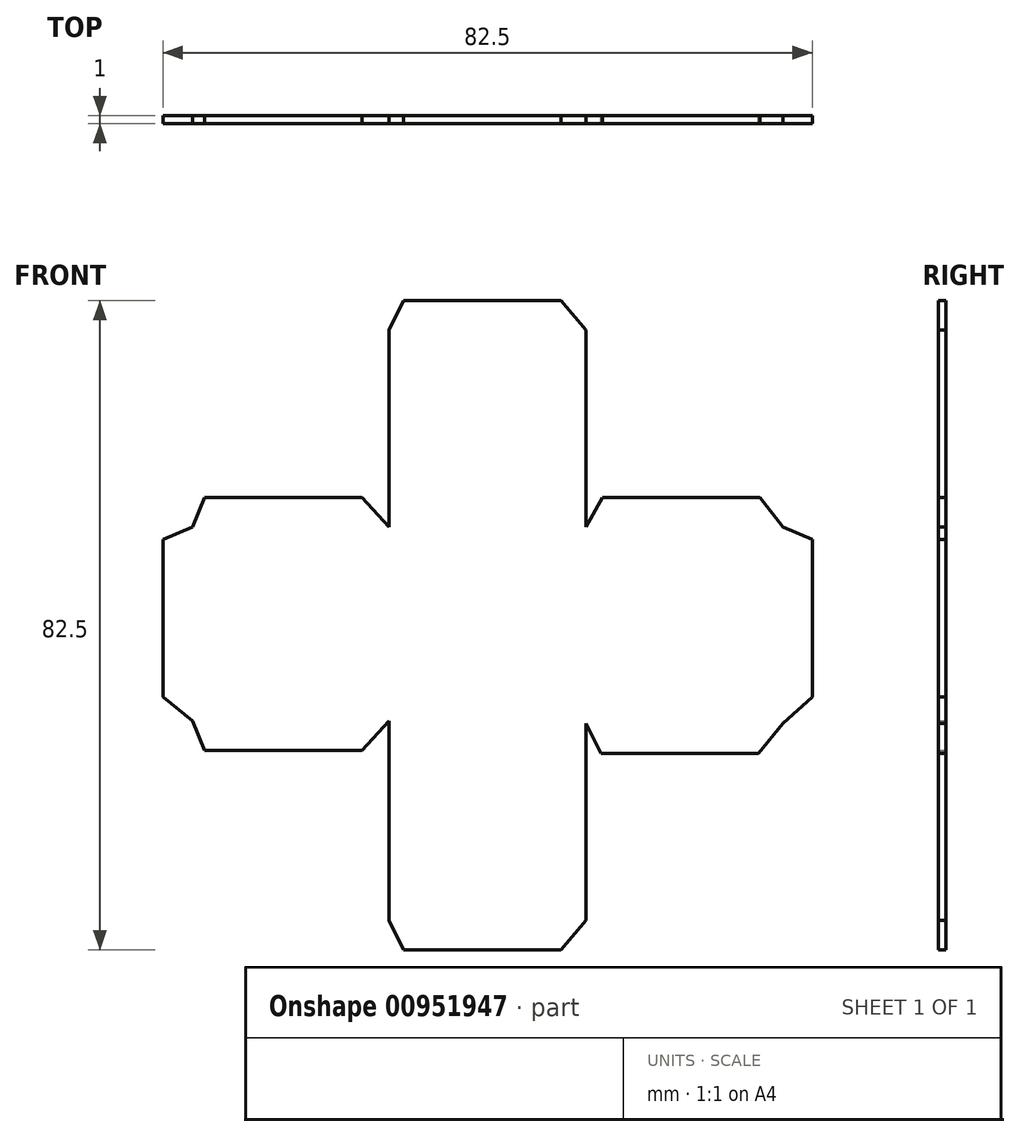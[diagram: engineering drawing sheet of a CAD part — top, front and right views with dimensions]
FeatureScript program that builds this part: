
annotation { "Feature Type Name" : "Feature", "Feature Type Description" : "" }
export const myFeature = defineFeature(function(context is Context, id is Id, definition is map)
    precondition{}
    {
        {
            var Q0;
            Q0=qCreatedBy(makeId("Front.planeOp"),FACE);
            var sketch = newSketch(context, id + "F0", { "sketchPlane" : qUnion([Q0])});
            skLineSegment(sketch, "E0", {"start": v(0, 0) * mm, "end": v(-25, 0) * mm});
            skLineSegment(sketch, "E1", {"start": v(-25, 0) * mm, "end": v(-25, 24.68) * mm});
            skLineSegment(sketch, "E2", {"start": v(-25, 24.68) * mm, "end": v(0, 24.68) * mm});
            skLineSegment(sketch, "E3", {"start": v(0, 24.68) * mm, "end": v(0, 49.68) * mm});
            skLineSegment(sketch, "E4", {"start": v(0, 49.68) * mm, "end": v(25, 49.68) * mm});
            skLineSegment(sketch, "E5", {"start": v(25, 49.68) * mm, "end": v(25, 24.68) * mm});
            skLineSegment(sketch, "E6", {"start": v(25, 24.68) * mm, "end": v(50, 24.68) * mm});
            skLineSegment(sketch, "E7", {"start": v(50, 24.68) * mm, "end": v(50, -0.32) * mm});
            skLineSegment(sketch, "E8", {"start": v(50, -0.32) * mm, "end": v(25, -0.32) * mm});
            skLineSegment(sketch, "E9", {"start": v(25, -0.32) * mm, "end": v(25, -25.32) * mm});
            skLineSegment(sketch, "E10", {"start": v(25, -25.32) * mm, "end": v(0, -25.32) * mm});
            skLineSegment(sketch, "E11", {"start": v(0, -25.32) * mm, "end": v(0, 0) * mm});
            skLineSegment(sketch, "E12", {"start": v(0, 49.68) * mm, "end": v(1.85, 53.43) * mm});
            skLineSegment(sketch, "E13", {"start": v(1.85, 53.43) * mm, "end": v(21.85, 53.43) * mm});
            skLineSegment(sketch, "E14", {"start": v(21.85, 53.43) * mm, "end": v(25, 49.68) * mm});
            skLineSegment(sketch, "E15", {"start": v(50, 24.68) * mm, "end": v(53.75, 23.1) * mm});
            skLineSegment(sketch, "E16", {"start": v(53.75, 23.1) * mm, "end": v(53.75, 3.1) * mm});
            skLineSegment(sketch, "E17", {"start": v(53.75, 3.1) * mm, "end": v(50, -0.32) * mm});
            skLineSegment(sketch, "E18", {"start": v(25, -25.32) * mm, "end": v(21.85, -29.07) * mm});
            skLineSegment(sketch, "E19", {"start": v(21.85, -29.07) * mm, "end": v(1.85, -29.07) * mm});
            skLineSegment(sketch, "E20", {"start": v(1.85, -29.07) * mm, "end": v(0, -25.32) * mm});
            skLineSegment(sketch, "E21", {"start": v(-25, 24.68) * mm, "end": v(-28.75, 23.1) * mm});
            skLineSegment(sketch, "E22", {"start": v(-28.75, 23.1) * mm, "end": v(-28.75, 3.1) * mm});
            skLineSegment(sketch, "E23", {"start": v(-28.75, 3.1) * mm, "end": v(-25, 0) * mm});
            skLineSegment(sketch, "E24", {"start": v(-25, 24.68) * mm, "end": v(-23.42, 28.43) * mm});
            skLineSegment(sketch, "E25", {"start": v(-23.42, 28.43) * mm, "end": v(-3.42, 28.43) * mm});
            skLineSegment(sketch, "E26", {"start": v(-3.42, 28.43) * mm, "end": v(0, 24.68) * mm});
            skLineSegment(sketch, "E27", {"start": v(-25, 0) * mm, "end": v(-23.42, -3.75) * mm});
            skLineSegment(sketch, "E28", {"start": v(-23.42, -3.75) * mm, "end": v(-3.42, -3.75) * mm});
            skLineSegment(sketch, "E29", {"start": v(-3.42, -3.75) * mm, "end": v(0, 0) * mm});
            skLineSegment(sketch, "E30", {"start": v(25, 24.68) * mm, "end": v(27.12, 28.43) * mm});
            skLineSegment(sketch, "E31", {"start": v(27.12, 28.43) * mm, "end": v(47.12, 28.43) * mm});
            skLineSegment(sketch, "E32", {"start": v(47.12, 28.43) * mm, "end": v(50, 24.68) * mm});
            skLineSegment(sketch, "E33", {"start": v(25, -0.32) * mm, "end": v(26.9, -4.07) * mm});
            skLineSegment(sketch, "E34", {"start": v(26.9, -4.07) * mm, "end": v(46.9, -4.07) * mm});
            skLineSegment(sketch, "E35", {"start": v(46.9, -4.07) * mm, "end": v(50, -0.32) * mm});
            skLineSegment(sketch, "E36", {"start": v(0, 0) * mm, "end": v(0, 24.68) * mm});
            skLineSegment(sketch, "E37", {"start": v(25, 24.68) * mm, "end": v(0, 24.68) * mm});
            skLineSegment(sketch, "E38", {"start": v(25, 24.68) * mm, "end": v(25, -0.32) * mm});
            skLineSegment(sketch, "E39", {"start": v(0, 0) * mm, "end": v(25, -0.32) * mm});
            skSolve(sketch);
        }
        {
            var Q0;
            Q0=makeQuery(id+"F0.imprint","IMPRINT",FACE,{"disambiguationData":[TD([[makeQuery(id+"F0.imprint","IMPRINT",EDGE,{"derivedFrom":sQuery(id+"F0.wireOp",EDGE,"E0")}),-1.0]])]});
            var Q1;
            Q1=makeQuery(id+"F0.imprint","IMPRINT",FACE,{"disambiguationData":[TD([[makeQuery(id+"F0.imprint","IMPRINT",EDGE,{"derivedFrom":sQuery(id+"F0.wireOp",EDGE,"E36")}),-1.0]])]});
            var Q2;
            Q2=makeQuery(id+"F0.imprint","IMPRINT",FACE,{"disambiguationData":[TD([[makeQuery(id+"F0.imprint","IMPRINT",EDGE,{"derivedFrom":sQuery(id+"F0.wireOp",EDGE,"E3")}),-1.0]])]});
            var Q3;
            Q3=makeQuery(id+"F0.imprint","IMPRINT",FACE,{"disambiguationData":[TD([[makeQuery(id+"F0.imprint","IMPRINT",EDGE,{"derivedFrom":sQuery(id+"F0.wireOp",EDGE,"E6")}),-1.0]])]});
            var Q4;
            Q4=makeQuery(id+"F0.imprint","IMPRINT",FACE,{"disambiguationData":[TD([[makeQuery(id+"F0.imprint","IMPRINT",EDGE,{"derivedFrom":sQuery(id+"F0.wireOp",EDGE,"E9")}),-1.0]])]});
            var Q5;
            Q5=makeQuery(id+"F0.imprint","IMPRINT",FACE,{"disambiguationData":[TD([[makeQuery(id+"F0.imprint","IMPRINT",EDGE,{"derivedFrom":sQuery(id+"F0.wireOp",EDGE,"E4")}),1.0]])]});
            var Q6;
            Q6=makeQuery(id+"F0.imprint","IMPRINT",FACE,{"disambiguationData":[TD([[makeQuery(id+"F0.imprint","IMPRINT",EDGE,{"derivedFrom":sQuery(id+"F0.wireOp",EDGE,"E2")}),1.0]])]});
            var Q7;
            Q7=makeQuery(id+"F0.imprint","IMPRINT",FACE,{"disambiguationData":[TD([[makeQuery(id+"F0.imprint","IMPRINT",EDGE,{"derivedFrom":sQuery(id+"F0.wireOp",EDGE,"E1")}),1.0]])]});
            var Q8;
            Q8=makeQuery(id+"F0.imprint","IMPRINT",FACE,{"disambiguationData":[TD([[makeQuery(id+"F0.imprint","IMPRINT",EDGE,{"derivedFrom":sQuery(id+"F0.wireOp",EDGE,"E0")}),1.0]])]});
            var Q9;
            Q9=makeQuery(id+"F0.imprint","IMPRINT",FACE,{"disambiguationData":[TD([[makeQuery(id+"F0.imprint","IMPRINT",EDGE,{"derivedFrom":sQuery(id+"F0.wireOp",EDGE,"E10")}),1.0]])]});
            var Q10;
            Q10=makeQuery(id+"F0.imprint","IMPRINT",FACE,{"disambiguationData":[TD([[makeQuery(id+"F0.imprint","IMPRINT",EDGE,{"derivedFrom":sQuery(id+"F0.wireOp",EDGE,"E8")}),1.0]])]});
            var Q11;
            Q11=makeQuery(id+"F0.imprint","IMPRINT",FACE,{"disambiguationData":[TD([[makeQuery(id+"F0.imprint","IMPRINT",EDGE,{"derivedFrom":sQuery(id+"F0.wireOp",EDGE,"E7")}),1.0]])]});
            var Q12;
            Q12=makeQuery(id+"F0.imprint","IMPRINT",FACE,{"disambiguationData":[TD([[makeQuery(id+"F0.imprint","IMPRINT",EDGE,{"derivedFrom":sQuery(id+"F0.wireOp",EDGE,"E6")}),1.0]])]});
            extrude(context, id + "F1", {"entities" : qUnion([Q0, Q1, Q2, Q3, Q4, Q5, Q6, Q7, Q8, Q9, Q10, Q11, Q12]), "depth" : 1 * mm, "offsetDistance" : 25 * mm});
        }
    });
